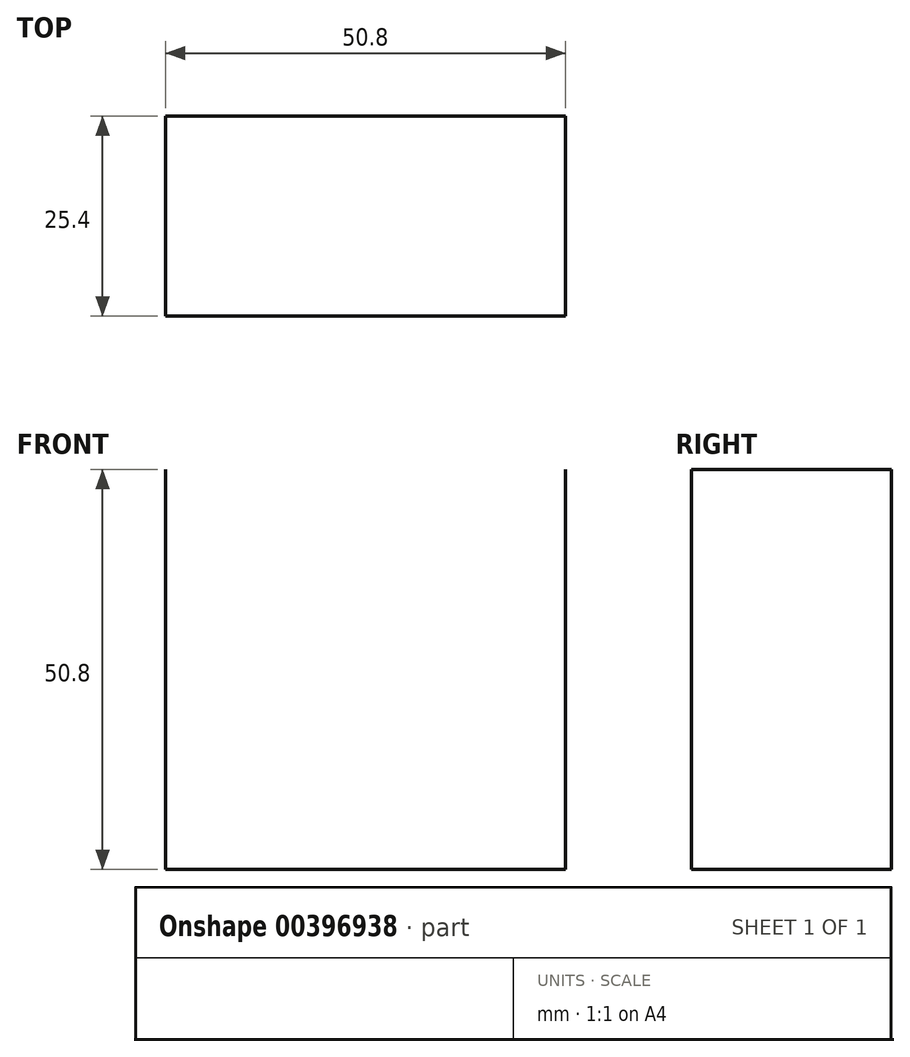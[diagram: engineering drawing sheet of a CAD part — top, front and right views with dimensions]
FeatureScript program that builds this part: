
annotation { "Feature Type Name" : "Feature", "Feature Type Description" : "" }
export const myFeature = defineFeature(function(context is Context, id is Id, definition is map)
    precondition{}
    {
        {
            var Q0;
            Q0=qCreatedBy(makeId("Front.planeOp"),FACE);
            var sketch = newSketch(context, id + "F0", { "sketchPlane" : qUnion([Q0])});
            skLineSegment(sketch, "E0.bottom", {"start": v(-50.8, 50.8) * mm, "end": v(0, 50.8) * mm});
            skLineSegment(sketch, "E0.top", {"start": v(-50.8, 0) * mm, "end": v(0, 0) * mm});
            skLineSegment(sketch, "E0.left", {"start": v(-50.8, 50.8) * mm, "end": v(-50.8, 0) * mm});
            skLineSegment(sketch, "E0.right", {"start": v(0, 50.8) * mm, "end": v(0, 0) * mm});
            skSolve(sketch);
        }
        {
            var Q0;
            Q0=sQuery(id+"F0.wireOp",EDGE,"E0.right");
            var Q1;
            Q1=sQuery(id+"F0.wireOp",EDGE,"E0.top");
            var Q2;
            Q2=sQuery(id+"F0.wireOp",EDGE,"E0.left");
            extrude(context, id + "F1", {"bodyType" : ToolBodyType.SURFACE, "surfaceEntities" : qUnion([Q0, Q1, Q2]), "depth" : 25.4 * mm});
        }
    });
